# Revit family: Furniture-Console_Table_Top-KALLISTA-Grid-P78574-1
name_source: partatom
category: Specialty Equipment
units: mm (PartAtom-declared; Revit-internal decimal feet)

## family parameters
Cut with Voids When Loaded = No
Host = Face
Maintain Annotation Orientation = No
OmniClass Number = 23.31.25.00
Part Type = Normal
Room Calculation Point = No
Round Connector Dimension = Use Diameter
Shared = No

## types (1)
- GM-Marmo Grigio Marble
    ADA Compliant = No
    Assembly Code = E20
    Date Modified = 06/21/2025
    Default Elevation = 48"
    Description = Console Table Top
    Finish = Kallista-Stone-GM-Marmo_Grigio_Marble
    Height = 1 3/16"
    Length = 27 1/4"
    Manufacturer = Kallista Co.
    Master Format 2014 = 06 41 93
    Master Format 2014 Name = Cabinet and Drawer Hardware
    Material = Stone
    Model = P78574-00-GM
    Product Documentation Link = https://techcomm.kohler.com
    Product Name = Grid
    Product Page URL = https://www.kallista.com
    Type = 1
    URL = https://www.kallista.com
    WaterSense Certified = No
    Width = 21 1/8"

## geometry (parser evidence)
native form markers: Sweep x5
no freeform markers — native parametric forms only
